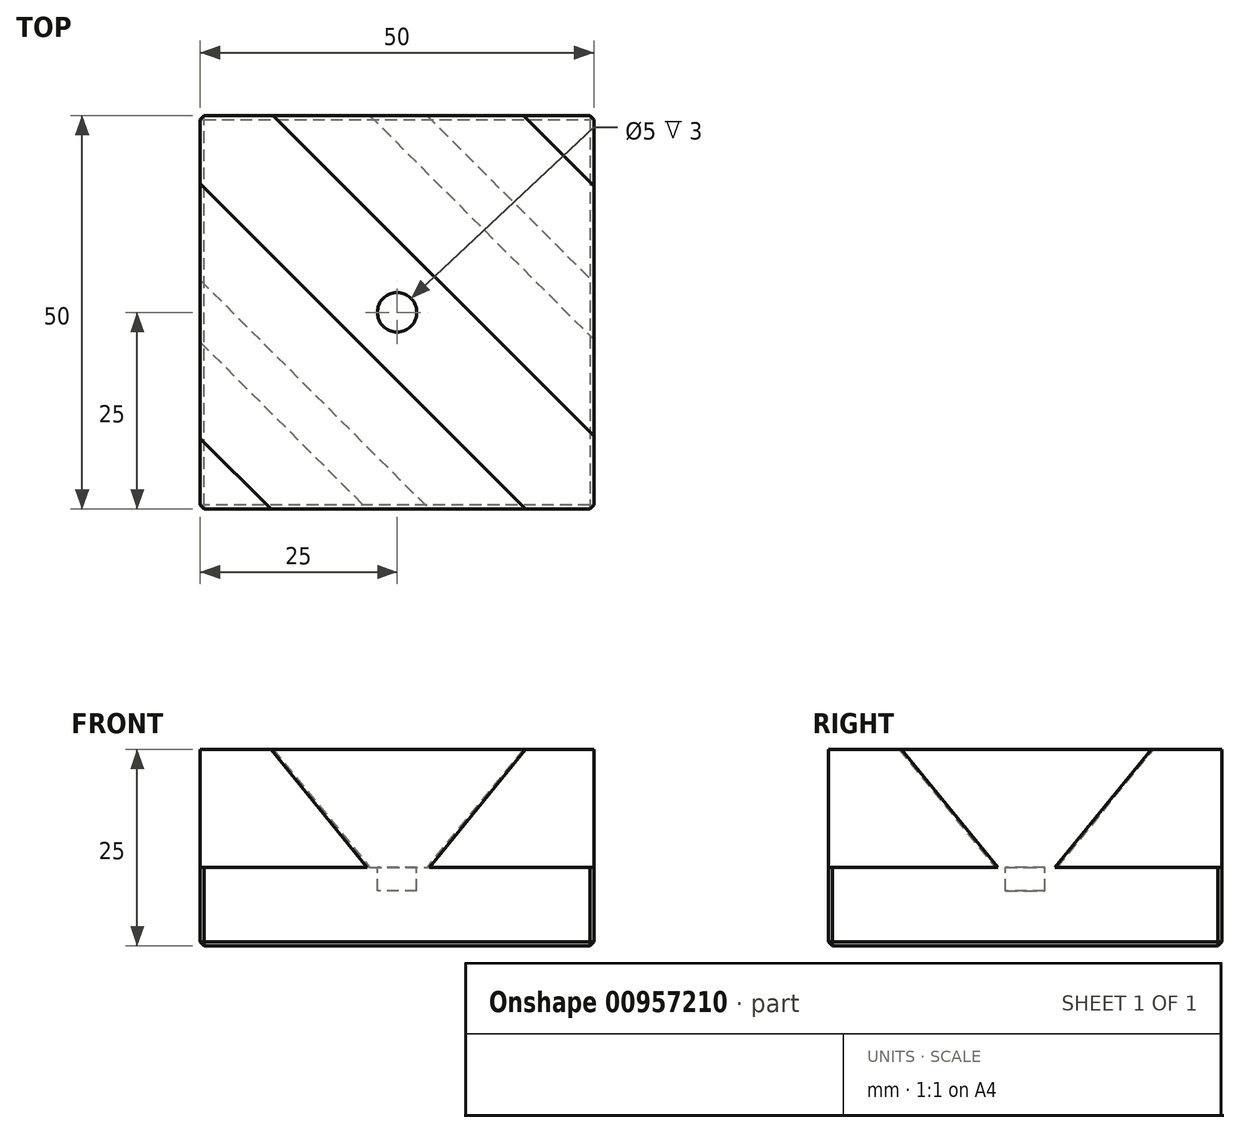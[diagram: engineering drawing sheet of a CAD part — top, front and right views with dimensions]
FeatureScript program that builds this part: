
annotation { "Feature Type Name" : "Feature", "Feature Type Description" : "" }
export const myFeature = defineFeature(function(context is Context, id is Id, definition is map)
    precondition{}
    {
        {
            var Q0;
            Q0=qCreatedBy(makeId("Top.planeOp"),FACE);
            var sketch = newSketch(context, id + "F0", { "sketchPlane" : qUnion([Q0])});
            skLineSegment(sketch, "E0.bottom", {"start": v(25, 25) * mm, "end": v(-25, 25) * mm});
            skLineSegment(sketch, "E0.top", {"start": v(25, -25) * mm, "end": v(-25, -25) * mm});
            skLineSegment(sketch, "E0.left", {"start": v(25, 25) * mm, "end": v(25, -25) * mm});
            skLineSegment(sketch, "E0.right", {"start": v(-25, 25) * mm, "end": v(-25, -25) * mm});
            skPoint(sketch, "E0.middle", {"position": v(0, 0) * mm});
            skSolve(sketch);
        }
        {
            var Q0;
            Q0=makeQuery(id+"F0.imprint","IMPRINT",FACE,{"disambiguationData":[TD([[makeQuery(id+"F0.imprint","IMPRINT",EDGE,{"derivedFrom":sQuery(id+"F0.wireOp",EDGE,"E0.bottom")}),1.0]])]});
            extrude(context, id + "F1", {"entities" : qUnion([Q0]), "depth" : 25 * mm, "offsetDistance" : 25 * mm});
        }
        {
            var Q0;
            Q0=makeQuery(id+"F1.opExtrude","SWEPT_EDGE",EDGE,{"disambiguationData":[OSD([sQuery(id+"F0.wireOp",EDGE,"E0.top"),sQuery(id+"F0.wireOp",EDGE,"E0.left")])]});
            cPlane(context, id + "F2", {"entities" : qUnion([Q0]), "cplaneType" : CPlaneType.LINE_ANGLE, "offset" : 25 * mm, "angle" : 45 * degree, "width" : 150 * mm, "height" : 150 * mm});
        }
        {
            var Q0;
            Q0=qCreatedBy(id+"F2.planeOp",FACE);
            var sketch = newSketch(context, id + "F3", { "sketchPlane" : qUnion([Q0])});
            skLineSegment(sketch, "E1.0", {"start": v(0, 25) * mm, "end": v(35.36, 25) * mm});
            skLineSegment(sketch, "E2.0", {"start": v(-35.36, 25) * mm, "end": v(0, 25) * mm});
            skLineSegment(sketch, "E3.0", {"start": v(35.36, 25) * mm, "end": v(35.36, 0) * mm});
            skLineSegment(sketch, "E4.0", {"start": v(-35.36, 25) * mm, "end": v(-35.36, 0) * mm});
            skLineSegment(sketch, "E5", {"start": v(29.02, 25) * mm, "end": v(20.36, 10) * mm});
            skLineSegment(sketch, "E6", {"start": v(20.36, 10) * mm, "end": v(35.36, 10) * mm});
            skLineSegment(sketch, "E7.MirrorCS", {"start": v(-29.02, 25) * mm, "end": v(-20.36, 10) * mm});
            skLineSegment(sketch, "E8.MirrorCS", {"start": v(-20.36, 10) * mm, "end": v(-35.36, 10) * mm});
            skLineSegment(sketch, "E9", {"start": v(-6.56, 25) * mm, "end": v(-15.22, 10) * mm});
            skLineSegment(sketch, "E10", {"start": v(-15.22, 10) * mm, "end": v(14.78, 10) * mm});
            skLineSegment(sketch, "E11", {"start": v(14.78, 10) * mm, "end": v(6.12, 25) * mm});
            skPoint(sketch, "E12.endSnap0", {"position": v(-0.22, 10) * mm});
            skSolve(sketch);
        }
        {
            var Q0;
            {var subQ3=sQuery(id+"F3.wireOp",EDGE,"E5");Q0=makeQuery(id+"F3.imprint","IMPRINT",FACE,{"disambiguationData":[TD([[makeQuery(id+"F3.imprint","IMPRINT",EDGE,{"derivedFrom":subQ3}),1.0]])]});}
            var Q1;
            {var subQ3=sQuery(id+"F3.wireOp",EDGE,"E7.MirrorCS");Q1=makeQuery(id+"F3.imprint","IMPRINT",FACE,{"disambiguationData":[TD([[makeQuery(id+"F3.imprint","IMPRINT",EDGE,{"derivedFrom":subQ3}),-1.0]])]});}
            var Q2;
            {var subQ4=sQuery(id+"F3.wireOp",EDGE,"E9");Q2=makeQuery(id+"F3.imprint","IMPRINT",FACE,{"disambiguationData":[TD([[makeQuery(id+"F3.imprint","IMPRINT",EDGE,{"derivedFrom":subQ4}),1.0]])]});}
            extrude(context, id + "F4", {"entities" : qUnion([Q0, Q1, Q2]), "operationType" : NewBodyOperationType.REMOVE, "endBound" : BoundingType.THROUGH_ALL, "depth" : 25 * mm, "offsetDistance" : 25 * mm});
        }
        {
            var Q0;
            Q0=makeQuery(id+"F4.boolean.opBoolean","COPY",FACE,{"derivedFrom":makeQuery(id+"F4.opExtrude","SWEPT_FACE",FACE,{"disambiguationData":[OSD([sQuery(id+"F3.wireOp",EDGE,"E10")])]})});
            var sketch = newSketch(context, id + "F5", { "sketchPlane" : qUnion([Q0])});
            skPoint(sketch, "E13.0", {"position": v(-25, -25) * mm});
            skPoint(sketch, "E14.0", {"position": v(25, 25) * mm});
            skLineSegment(sketch, "E15.bottom", {"start": v(-25, -25) * mm, "end": v(25, -25) * mm});
            skLineSegment(sketch, "E15.top", {"start": v(-25, 25) * mm, "end": v(25, 25) * mm});
            skLineSegment(sketch, "E15.left", {"start": v(-25, -25) * mm, "end": v(-25, 25) * mm});
            skLineSegment(sketch, "E15.right", {"start": v(25, -25) * mm, "end": v(25, 25) * mm});
            skSolve(sketch);
        }
        {
            var Q0;
            Q0 = qSketchRegion(id + "F5", true);
            extrude(context, id + "F6", {"entities" : qUnion([Q0]), "depth" : 25 * mm, "offsetDistance" : 25 * mm});
        }
        {
            var Q0;
            Q0=makeQuery(id+"F1.opExtrude","SWEPT_BODY",BODY,{"disambiguationData":[OSD([sQuery(id+"F0.wireOp",EDGE,"E0.bottom"),sQuery(id+"F0.wireOp",EDGE,"E0.top"),sQuery(id+"F0.wireOp",EDGE,"E0.left"),sQuery(id+"F0.wireOp",EDGE,"E0.right")])]});
            var Q1;
            Q1=makeQuery(id+"F6.opExtrude","SWEPT_BODY",BODY,{"disambiguationData":[OSD([sQuery(id+"F5.wireOp",EDGE,"E15.bottom"),sQuery(id+"F5.wireOp",EDGE,"E15.top"),sQuery(id+"F5.wireOp",EDGE,"E15.left"),sQuery(id+"F5.wireOp",EDGE,"E15.right")])]});
            booleanBodies(context, id + "F7", {"operationType" : BooleanOperationType.SUBTRACTION, "tools" : qUnion([Q0]), "targets" : qUnion([Q1]), "keepTools" : true});
        }
        {
            var Q0;
            Q0=makeQuery(id+"F6.opExtrude","SWEPT_BODY",BODY,{"disambiguationData":[OSD([sQuery(id+"F5.wireOp",EDGE,"E15.bottom"),sQuery(id+"F5.wireOp",EDGE,"E15.top"),sQuery(id+"F5.wireOp",EDGE,"E15.left"),sQuery(id+"F5.wireOp",EDGE,"E15.right")])]});
            var Q1;
            Q1=makeQuery(id+"F1.opExtrude","CAP_EDGE",EDGE,{"disambiguationData":[OSD([sQuery(id+"F0.wireOp",EDGE,"E0.top")])],"isStart":true});
            transform(context, id + "F8", {"entities" : qUnion([Q0]), "transformType" : TransformType.TRANSLATION_DISTANCE, "transformDirection" : qUnion([Q1]), "distance" : 55 * mm, "makeCopy" : false});
        }
        {
            var Q0;
            Q0=makeQuery(id+"F1.opExtrude","SWEPT_EDGE",EDGE,{"disambiguationData":[OSD([sQuery(id+"F0.wireOp",EDGE,"E0.bottom"),sQuery(id+"F0.wireOp",EDGE,"E0.right")])]});
            var Q1;
            Q1=makeQuery(id+"F1.opExtrude","SWEPT_EDGE",EDGE,{"disambiguationData":[OSD([sQuery(id+"F0.wireOp",EDGE,"E0.bottom"),sQuery(id+"F0.wireOp",EDGE,"E0.left")])]});
            var Q2;
            Q2=makeQuery(id+"F1.opExtrude","SWEPT_EDGE",EDGE,{"disambiguationData":[OSD([sQuery(id+"F0.wireOp",EDGE,"E0.top"),sQuery(id+"F0.wireOp",EDGE,"E0.left")])]});
            var Q3;
            Q3=makeQuery(id+"F1.opExtrude","SWEPT_EDGE",EDGE,{"disambiguationData":[OSD([sQuery(id+"F0.wireOp",EDGE,"E0.top"),sQuery(id+"F0.wireOp",EDGE,"E0.right")])]});
            var Q4;
            Q4=makeQuery(id+"F1.opExtrude","CAP_EDGE",EDGE,{"disambiguationData":[OSD([sQuery(id+"F0.wireOp",EDGE,"E0.top")])],"isStart":true});
            var Q5;
            Q5=makeQuery(id+"F1.opExtrude","CAP_EDGE",EDGE,{"disambiguationData":[OSD([sQuery(id+"F0.wireOp",EDGE,"E0.left")])],"isStart":true});
            var Q6;
            Q6=makeQuery(id+"F1.opExtrude","CAP_EDGE",EDGE,{"disambiguationData":[OSD([sQuery(id+"F0.wireOp",EDGE,"E0.bottom")])],"isStart":true});
            var Q7;
            Q7=makeQuery(id+"F1.opExtrude","CAP_EDGE",EDGE,{"disambiguationData":[OSD([sQuery(id+"F0.wireOp",EDGE,"E0.right")])],"isStart":true});
            chamfer(context, id + "F9", {"entities" : qUnion([Q0, Q1, Q2, Q3, Q4, Q5, Q6, Q7]), "width" : .5 * mm, "tangentPropagation" : true});
        }
        {
            var Q0;
            Q0=makeQuery(id+"F6.opExtrude","SWEPT_BODY",BODY,{"disambiguationData":[OSD([sQuery(id+"F5.wireOp",EDGE,"E15.bottom"),sQuery(id+"F5.wireOp",EDGE,"E15.top"),sQuery(id+"F5.wireOp",EDGE,"E15.left"),sQuery(id+"F5.wireOp",EDGE,"E15.right")])]});
            deleteBodies(context, id + "F10", {"entities" : qUnion([Q0])});
        }
        {
            var Q0;
            Q0=makeQuery(id+"F4.boolean.opBoolean","COPY",FACE,{"derivedFrom":makeQuery(id+"F4.opExtrude","SWEPT_FACE",FACE,{"disambiguationData":[OSD([sQuery(id+"F3.wireOp",EDGE,"E10")])]})});
            var sketch = newSketch(context, id + "F11", { "sketchPlane" : qUnion([Q0])});
            skCircle(sketch, "E16", {"center": v(0, 0) * mm, "radius": 2.5 * mm});
            skSolve(sketch);
        }
        {
            var Q0;
            Q0=makeQuery(id+"F11.imprint","IMPRINT",FACE,{"disambiguationData":[TD([[makeQuery(id+"F11.imprint","IMPRINT",EDGE,{"derivedFrom":sQuery(id+"F11.wireOp",EDGE,"E16")}),1.0]])]});
            extrude(context, id + "F12", {"entities" : qUnion([Q0]), "operationType" : NewBodyOperationType.REMOVE, "oppositeDirection" : true, "depth" : 3 * mm, "offsetDistance" : 25 * mm});
        }
    });
